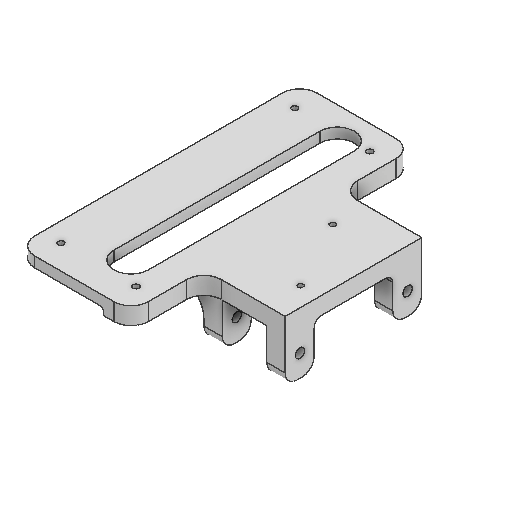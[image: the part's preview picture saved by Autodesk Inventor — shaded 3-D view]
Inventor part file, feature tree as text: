
AUTODESK INVENTOR PART (.ipt)
format: ipt  version: 2025 (Build 290162000, 162)  size: 346,112 bytes
history: native  units: mm
features: projected_geometry x9, extrude x8, sketch x8, fillet x6, other x3, reference x2
ambient origin geometry x8: Origin, YZ Plane, XZ Plane, XY Plane, X Axis, Y Axis, Z Axis, Center Point
bodies: Solid1 (feature_tree)
feature tree (36):
  extrude  "Extrusion1"  Depth=10.0mm TaperAngle=0.0deg
  extrude  "Extrusion2"  Depth=43.5mm
  extrude  "Extrusion3"  Depth=25.8mm
  extrude  "Extrusion5"  Depth=5.5mm
  fillet  "Fillet4"  [1 undecoded]
  extrude  "Extrusion6"  TaperAngle=0.0deg  [1 undecoded]
  fillet  "Fillet5"  Radius=4.0mm
  fillet  "Fillet6"  [1 undecoded]
  extrude  "Extrusion7"  Depth=10.0mm
  fillet  "Fillet7"  Radius=10.0mm
  fillet  "Fillet8"  Radius=10.0mm
  extrude  "Extrusion8"  Depth=10.0mm
  fillet  "Fillet9"  Radius=1.0mm
  extrude  "Extrusion4"  Depth=10.0mm TaperAngle=0.0deg
  sketch  "Sketch1"  dims[d0=3.5mm d1=10.0mm d2=0.0mm]
  sketch  "Sketch2"  dims[d3=135.5mm d4=43.5mm]
  reference  "Reference1"
  reference  "Reference2"
  sketch  "Sketch3"  dims[d5=0.0mm d6=0.0mm d7=25.8mm]
  projected_geometry  "Projected Loop1"
  sketch  "Sketch4"  dims[d8=25.4mm d9=0.0mm d13=5.5mm d14=0.0mm d15=0.0mm]
  projected_geometry  "Projected Loop2"
  projected_geometry  "Projected Loop3"
  sketch  "Sketch5"  dims[d16=5.5mm d17=0.0mm d18=0.0mm d19=4.0mm d20=0.0mm d21=0.0mm]
  projected_geometry  "Projected Loop4"
  projected_geometry  "Projected Loop5"
  sketch  "Sketch6"  dims[d22=10.0mm d23=15.0mm d24=10.0mm d25=10.0mm]
  projected_geometry  "Projected Loop6"
  sketch  "Sketch7"  dims[d26=10.0mm d27=0.0mm d28=7.0mm d29=1.0mm]
  sketch  "Sketch8"  dims[d31=6.0mm d32=10.0mm d33=0.0mm d34=2.0mm d35=12.7mm d36=12.7mm d37=0.5mm d38=0.872665mm d39=0.5mm d40=0.872665mm]
  projected_geometry  "Projected Loop7"
  projected_geometry  "Projected Loop8"
  projected_geometry  "Projected Loop9"
  other  "<userpath>\Desktop\puppycat\woodhouseMK1.iam"
  other  "woodhouseMK1.iam"
  other  "50W 2Ohm Power Resistor:1"
note: 3 required parameter values undecoded (feature->parameter linkage not recoverable at this tier; creation-order binding heuristic only, values carry confidence <= 0.55)
